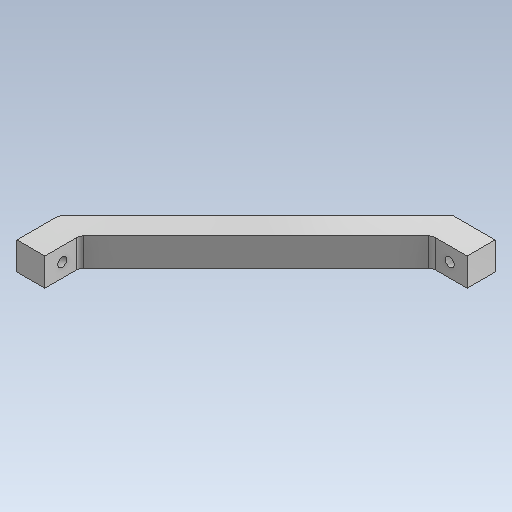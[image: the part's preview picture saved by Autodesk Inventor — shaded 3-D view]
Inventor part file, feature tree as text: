
AUTODESK INVENTOR PART (.ipt)
format: ipt  version: 2020 (Build 240168000, 168)  size: 134,144 bytes
history: native  units: mm
features: sketch x3, hole x2, extrude x1, fillet x1
ambient origin geometry x8: Origin, YZ Plane, XZ Plane, XY Plane, X Axis, Y Axis, Z Axis, Center Point
bodies: Solid1 (feature_tree)
feature tree (7):
  extrude  "Extrusion1"  Depth=30.0mm
  sketch  "Sketch2"  dims[d4=45.0deg d5=200.0mm]
  sketch  "Sketch3"  dims[d6=20.0mm d7=20.0mm d9=20.0mm d10=0.0mm d11=6.5mm d12=6.0mm d13=4.0mm d14=2.0mm d15=90.0deg d16=8.0mm d17=20.594885mm d18=6.5mm d19=6.0mm d20=4.0mm d21=2.0mm d22=90.0deg d23=8.0mm d24=20.594885mm d25=5.0mm d27=30.0mm d29=5.0mm]
  hole  "Hole1"  [1 undecoded]
  hole  "Hole2"  [1 undecoded]
  fillet  "Fillet1"  Radius=20.0mm
  sketch  "Sketch1"  dims[d0=90.0deg d1=30.0mm]
note: 2 required parameter values undecoded (feature->parameter linkage not recoverable at this tier; creation-order binding heuristic only, values carry confidence <= 0.55)
